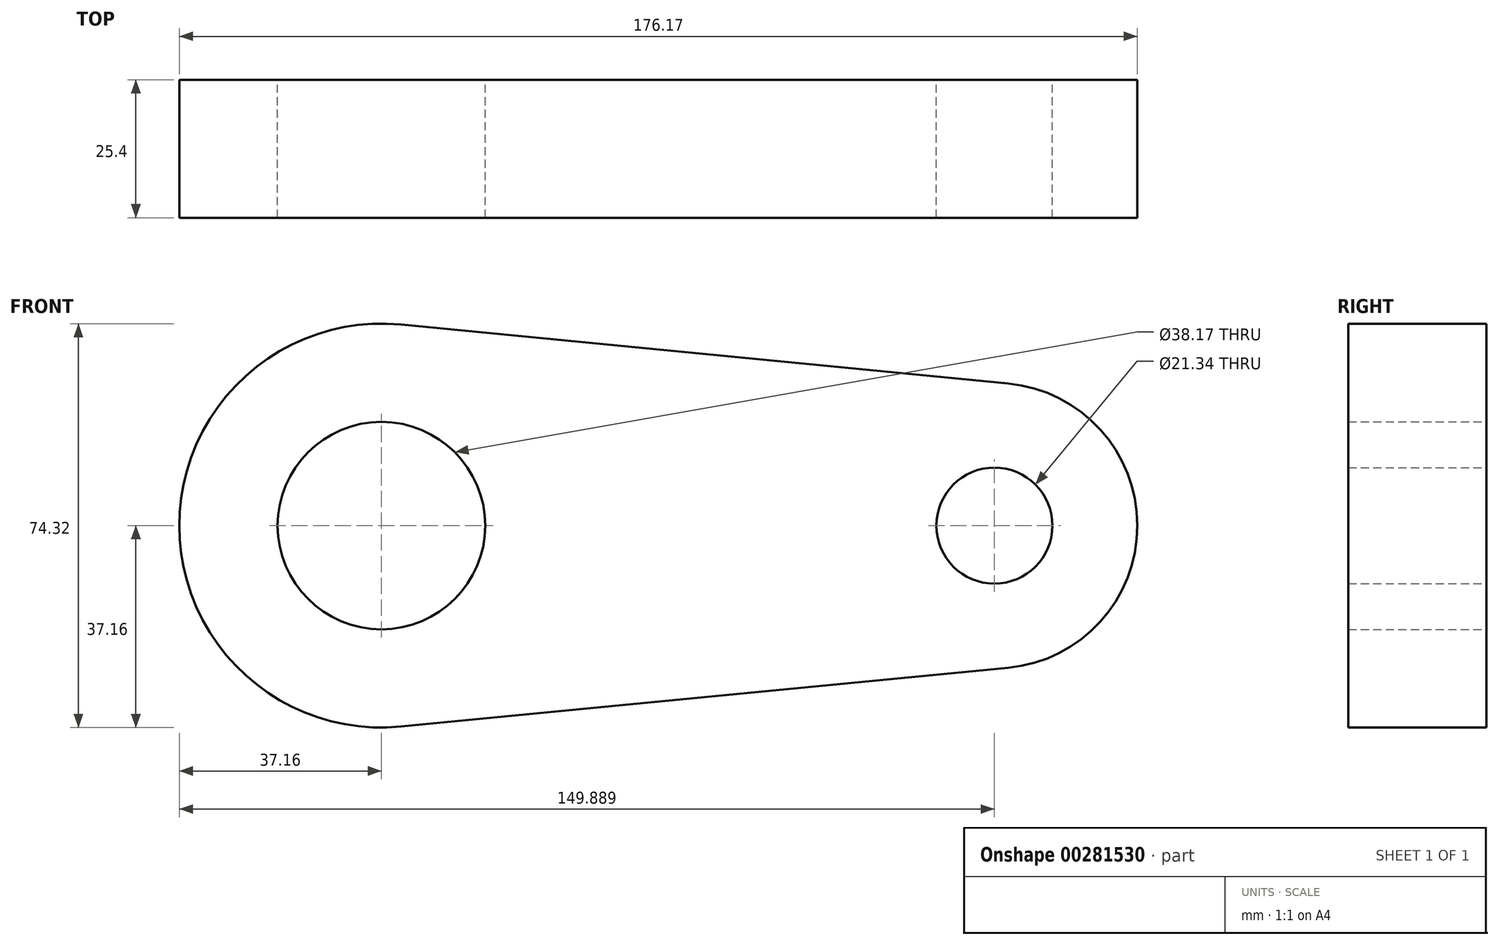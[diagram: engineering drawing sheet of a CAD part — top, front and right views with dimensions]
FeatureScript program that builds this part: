
annotation { "Feature Type Name" : "Feature", "Feature Type Description" : "" }
export const myFeature = defineFeature(function(context is Context, id is Id, definition is map)
    precondition{}
    {
        {
            var Q0;
            Q0=qCreatedBy(makeId("Front.planeOp"),FACE);
            var sketch = newSketch(context, id + "F0", { "sketchPlane" : qUnion([Q0])});
            skCircle(sketch, "E0", {"center": v(0, 0) * mm, "radius": 19.09 * mm});
            skCircle(sketch, "E1", {"center": v(112.73, 0) * mm, "radius": 10.67 * mm});
            skArc(sketch, "E2", {"start": v(3.59, 37) * mm, "mid": v(-37.16, 0) * mm, "end": v(3.59, -37) * mm});
            skArc(sketch, "E3", {"start": v(115.27, -26.16) * mm, "mid": v(139.01, 0) * mm, "end": v(115.27, 26.16) * mm});
            skLineSegment(sketch, "E4", {"start": v(3.59, 37) * mm, "end": v(115.27, 26.16) * mm});
            skLineSegment(sketch, "E5", {"start": v(3.59, -37) * mm, "end": v(115.27, -26.16) * mm});
            skSolve(sketch);
        }
        {
            var Q0;
            Q0=makeQuery(id+"F0.imprint","IMPRINT",FACE,{"disambiguationData":[TD([[makeQuery(id+"F0.imprint","IMPRINT",EDGE,{"derivedFrom":sQuery(id+"F0.wireOp",EDGE,"E0")}),-1.0]])]});
            extrude(context, id + "F1", {"entities" : qUnion([Q0]), "depth" : 25.4 * mm});
        }
    });
